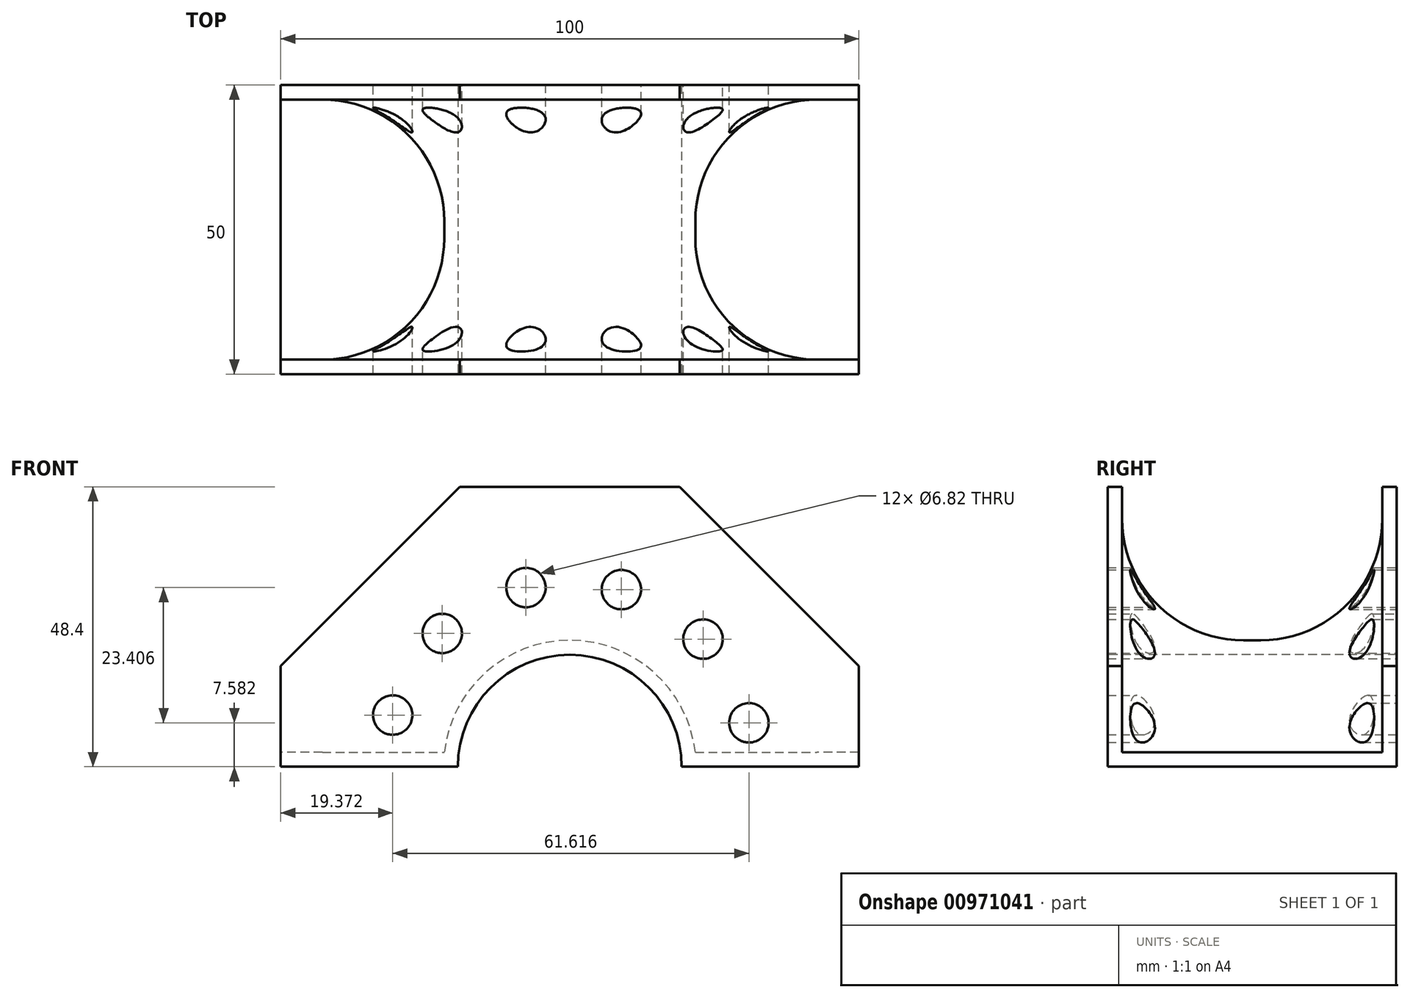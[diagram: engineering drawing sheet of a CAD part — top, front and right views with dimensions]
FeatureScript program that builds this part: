
annotation { "Feature Type Name" : "Feature", "Feature Type Description" : "" }
export const myFeature = defineFeature(function(context is Context, id is Id, definition is map)
    precondition{}
    {
        {
            var Q0;
            Q0=qCreatedBy(makeId("Top.planeOp"),FACE);
            var sketch = newSketch(context, id + "F0", { "sketchPlane" : qUnion([Q0])});
            skLineSegment(sketch, "E0.bottom", {"start": v(50, -25) * mm, "end": v(-50, -25) * mm});
            skLineSegment(sketch, "E0.top", {"start": v(50, 25) * mm, "end": v(-50, 25) * mm});
            skLineSegment(sketch, "E0.left", {"start": v(50, -25) * mm, "end": v(50, 25) * mm});
            skLineSegment(sketch, "E0.right", {"start": v(-50, -25) * mm, "end": v(-50, 25) * mm});
            skPoint(sketch, "E0.middle", {"position": v(0, 0) * mm});
            skSolve(sketch);
        }
        {
            var Q0;
            Q0=makeQuery(id+"F0.imprint","IMPRINT",FACE,{"disambiguationData":[TD([[makeQuery(id+"F0.imprint","IMPRINT",EDGE,{"derivedFrom":sQuery(id+"F0.wireOp",EDGE,"E0.bottom")}),-1.0]])]});
            extrude(context, id + "F1", {"entities" : qUnion([Q0]), "depth" : 48.4 * mm, "offsetDistance" : 25 * mm});
        }
        {
            var Q0;
            Q0=makeQuery(id+"F1.opExtrude","SWEPT_FACE",FACE,{"disambiguationData":[OSD([sQuery(id+"F0.wireOp",EDGE,"E0.bottom")])]});
            var sketch = newSketch(context, id + "F2", { "sketchPlane" : qUnion([Q0])});
            skCircle(sketch, "E1", {"center": v(0, 0) * mm, "radius": 19.35 * mm});
            skSolve(sketch);
        }
        {
            var Q0;
            {var subQ0=sQuery(id+"F2.wireOp",EDGE,"E1");var subQ1=makeQuery(id+"F1.opExtrude","CAP_EDGE",EDGE,{"disambiguationData":[OSD([sQuery(id+"F0.wireOp",EDGE,"E0.bottom")])],"isStart":true});var subQ2=makeQuery(id+"F2.imprint","INTERSECT",VERTEX,{"disambiguationData":[OD(0.0)],"derivedFrom":[subQ1,subQ0]});Q0=makeQuery(id+"F2.imprint","IMPRINT",FACE,{"disambiguationData":[TD([[makeQuery(id+"F2.imprint","IMPRINT",EDGE,{"disambiguationData":[TD([[subQ2,-1.0]])],"derivedFrom":subQ0}),1.0]])]});}
            var Q1;
            {var subQ0=sQuery(id+"F2.wireOp",EDGE,"E1");var subQ1=makeQuery(id+"F1.opExtrude","CAP_EDGE",EDGE,{"disambiguationData":[OSD([sQuery(id+"F0.wireOp",EDGE,"E0.bottom")])],"isStart":true});var subQ2=makeQuery(id+"F2.imprint","INTERSECT",VERTEX,{"disambiguationData":[OD(0.0)],"derivedFrom":[subQ1,subQ0]});Q1=makeQuery(id+"F2.imprint","IMPRINT",FACE,{"disambiguationData":[TD([[makeQuery(id+"F2.imprint","IMPRINT",EDGE,{"disambiguationData":[TD([[subQ2,1.0]])],"derivedFrom":subQ0}),1.0]])]});}
            extrude(context, id + "F3", {"entities" : qUnion([Q0, Q1]), "operationType" : NewBodyOperationType.REMOVE, "oppositeDirection" : true, "depth" : 94.3 * mm, "offsetDistance" : 25 * mm});
        }
        {
            var Q0;
            Q0=makeQuery(id+"F1.opExtrude","CAP_FACE",FACE,{"disambiguationData":[OSD([sQuery(id+"F0.wireOp",EDGE,"E0.bottom"),sQuery(id+"F0.wireOp",EDGE,"E0.top"),sQuery(id+"F0.wireOp",EDGE,"E0.left"),sQuery(id+"F0.wireOp",EDGE,"E0.right")])],"isStart":false});
            var Q1;
            Q1=makeQuery(id+"F1.opExtrude","SWEPT_FACE",FACE,{"disambiguationData":[OSD([sQuery(id+"F0.wireOp",EDGE,"E0.right")])]});
            var Q2;
            Q2=makeQuery(id+"F1.opExtrude","SWEPT_FACE",FACE,{"disambiguationData":[OSD([sQuery(id+"F0.wireOp",EDGE,"E0.left")])]});
            shell(context, id + "F4", {"entities" : qUnion([Q0, Q1, Q2]), "thickness" : 2.5 * mm});
        }
        {
            var Q0;
            Q0=makeQuery(id+"F4.opShell","OFFSET_EDGE",EDGE,{"disambiguationData":[OSD([sQuery(id+"F0.wireOp",EDGE,"E0.top"),sQuery(id+"F2.wireOp",EDGE,"E1")])]});
            var Q1;
            Q1=makeQuery(id+"F4.opShell","OFFSET_EDGE",EDGE,{"disambiguationData":[OSD([sQuery(id+"F2.wireOp",EDGE,"E1")])]});
            fillet(context, id + "F5", {"entities" : qUnion([Q0, Q1]), "radius" : 21 * mm, "tangentPropagation" : true, "allowEdgeOverflow" : false});
        }
        {
            var Q0;
            Q0=makeQuery(id+"F1.opExtrude","CAP_EDGE",EDGE,{"disambiguationData":[OSD([sQuery(id+"F0.wireOp",EDGE,"E0.right")])],"isStart":false});
            var Q1;
            {var subQ0=sQuery(id+"F0.wireOp",EDGE,"E0.right");Q1=makeQuery(id+"F4.opShell","OFFSET_EDGE",EDGE,{"disambiguationData":[OSD([subQ0]),TDD([makeQuery(id+"F1.opExtrude","CAP_EDGE",EDGE,{"disambiguationData":[OSD([subQ0])],"isStart":false})])]});}
            var Q2;
            {var subQ0=sQuery(id+"F0.wireOp",EDGE,"E0.left");Q2=makeQuery(id+"F4.opShell","OFFSET_EDGE",EDGE,{"disambiguationData":[OSD([subQ0]),TDD([makeQuery(id+"F1.opExtrude","CAP_EDGE",EDGE,{"disambiguationData":[OSD([subQ0])],"isStart":false})])]});}
            var Q3;
            Q3=makeQuery(id+"F1.opExtrude","CAP_EDGE",EDGE,{"disambiguationData":[OSD([sQuery(id+"F0.wireOp",EDGE,"E0.left")])],"isStart":false});
            chamfer(context, id + "F6", {"entities" : qUnion([Q0, Q1, Q2, Q3]), "width" : 31 * mm, "tangentPropagation" : true});
        }
        {
            var Q0;
            Q0=makeQuery(id+"F1.opExtrude","SWEPT_FACE",FACE,{"disambiguationData":[OSD([sQuery(id+"F0.wireOp",EDGE,"E0.top")])]});
            var sketch = newSketch(context, id + "F7", { "sketchPlane" : qUnion([Q0])});
            skCircle(sketch, "E2", {"center": v(0, 0) * mm, "radius": 31.9 * mm, "construction": true});
            skCircle(sketch, "E3", {"center": v(-30.99, 7.58) * mm, "radius": 3.4 * mm});
            skCircle(sketch, "E4.1.0", {"center": v(-23.05, 22.06) * mm, "radius": 3.4 * mm});
            skCircle(sketch, "E4.2.0", {"center": v(-8.93, 30.63) * mm, "radius": 3.4 * mm});
            skCircle(sketch, "E4.3.0", {"center": v(7.58, 30.99) * mm, "radius": 3.4 * mm});
            skCircle(sketch, "E4.4.0", {"center": v(22.06, 23.05) * mm, "radius": 3.4 * mm});
            skCircle(sketch, "E4.5.0", {"center": v(30.63, 8.93) * mm, "radius": 3.4 * mm});
            skLineSegment(sketch, "E4.anchor1", {"start": v(0, 0) * mm, "end": v(-30.99, 7.58) * mm, "construction": true});
            skLineSegment(sketch, "E4.anchor2", {"start": v(0, 0) * mm, "end": v(30.63, 8.93) * mm, "construction": true});
            skSolve(sketch);
        }
        {
            var Q0;
            Q0 = qSketchRegion(id + "F7", true);
            extrude(context, id + "F8", {"entities" : qUnion([Q0]), "operationType" : NewBodyOperationType.REMOVE, "oppositeDirection" : true, "depth" : 84.7 * mm, "offsetDistance" : 25 * mm});
        }
    });
